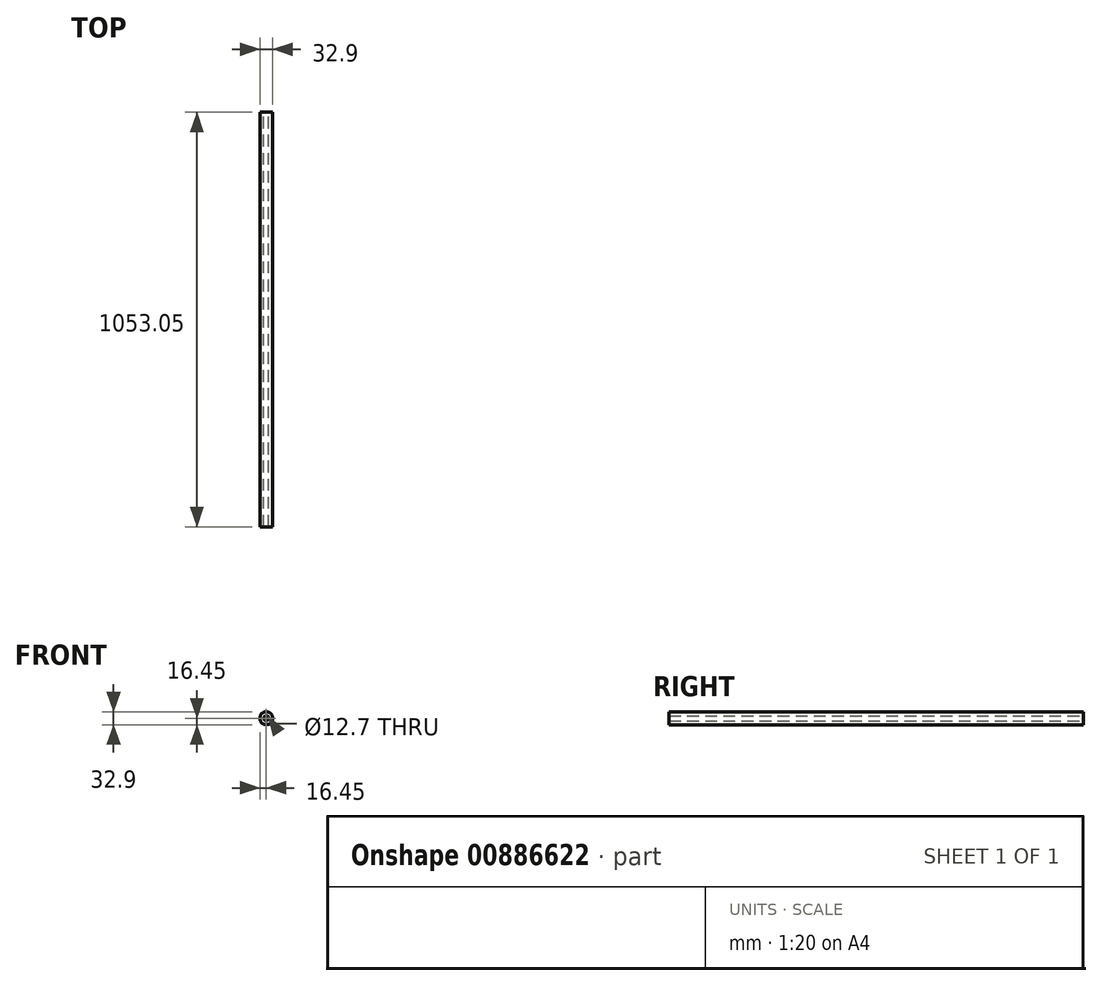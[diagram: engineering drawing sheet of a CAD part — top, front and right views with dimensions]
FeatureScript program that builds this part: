
annotation { "Feature Type Name" : "Feature", "Feature Type Description" : "" }
export const myFeature = defineFeature(function(context is Context, id is Id, definition is map)
    precondition{}
    {
        {
            assignVariable(context, id + "F0", {"name" : "StrutLength", "anyValue" : 1053.05 * mm});
        }
        {
            var Q0;
            Q0=qCreatedBy(makeId("Front.planeOp"),FACE);
            var sketch = newSketch(context, id + "F1", { "sketchPlane" : qUnion([Q0])});
            skCircle(sketch, "E0", {"center": v(0, 0) * mm, "radius": 6.35 * mm});
            skCircle(sketch, "E1", {"center": v(0, 0) * mm, "radius": 16.45 * mm});
            skSolve(sketch);
        }
        {
            var Q0;
            Q0=makeQuery(id+"F1.imprint","IMPRINT",FACE,{"disambiguationData":[TD([[makeQuery(id+"F1.imprint","IMPRINT",EDGE,{"derivedFrom":sQuery(id+"F1.wireOp",EDGE,"E0")}),-1.0]])]});
            extrude(context, id + "F2", {"entities" : qUnion([Q0]), "depth" : getVariable(context, 'StrutLength'), "offsetDistance" : 25.4 * mm});
        }
    });
